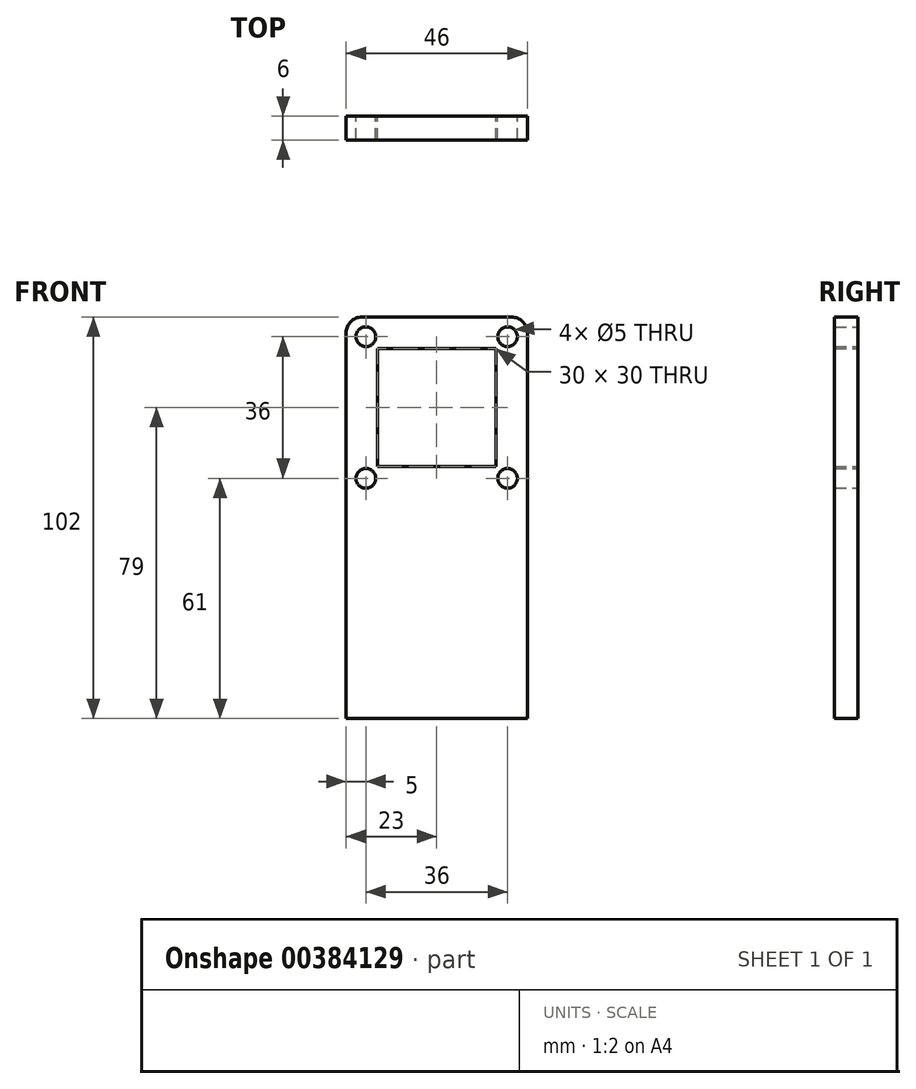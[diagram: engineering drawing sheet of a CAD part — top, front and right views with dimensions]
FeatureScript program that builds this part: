
annotation { "Feature Type Name" : "Feature", "Feature Type Description" : "" }
export const myFeature = defineFeature(function(context is Context, id is Id, definition is map)
    precondition{}
    {
        {
            var Q0;
            Q0=qCreatedBy(makeId("Front.planeOp"),FACE);
            var sketch = newSketch(context, id + "F0", { "sketchPlane" : qUnion([Q0])});
            skLineSegment(sketch, "E0.bottom", {"start": v(19, 51) * mm, "end": v(-19, 51) * mm});
            skLineSegment(sketch, "E0.top", {"start": v(23, -51) * mm, "end": v(-23, -51) * mm});
            skLineSegment(sketch, "E0.left", {"start": v(23, 47) * mm, "end": v(23, -51) * mm});
            skLineSegment(sketch, "E0.right", {"start": v(-23, 47) * mm, "end": v(-23, -51) * mm});
            skPoint(sketch, "E0.middle", {"position": v(0, 0) * mm});
            skLineSegment(sketch, "E1.bottom", {"start": v(15, 43) * mm, "end": v(-15, 43) * mm});
            skLineSegment(sketch, "E1.top", {"start": v(15, 13) * mm, "end": v(-15, 13) * mm});
            skLineSegment(sketch, "E1.left", {"start": v(15, 43) * mm, "end": v(15, 13) * mm});
            skLineSegment(sketch, "E1.right", {"start": v(-15, 43) * mm, "end": v(-15, 13) * mm});
            skPoint(sketch, "E1.middle", {"position": v(0, 28) * mm});
            skCircle(sketch, "E2", {"center": v(-18, 46) * mm, "radius": 2.5 * mm});
            skPoint(sketch, "E3.visualSharp", {"position": v(-23, 51) * mm});
            skArc(sketch, "E3.filletArc", {"start": v(-19, 51) * mm, "mid": v(-21.83, 49.83) * mm, "end": v(-23, 47) * mm});
            skPoint(sketch, "E4.visualSharp", {"position": v(23, 51) * mm});
            skArc(sketch, "E4.filletArc", {"start": v(23, 47) * mm, "mid": v(21.83, 49.83) * mm, "end": v(19, 51) * mm});
            skCircle(sketch, "E5.0.1.0", {"center": v(-18, 10) * mm, "radius": 2.5 * mm});
            skCircle(sketch, "E5.1.0.0", {"center": v(18, 46) * mm, "radius": 2.5 * mm});
            skCircle(sketch, "E5.1.1.0", {"center": v(18, 10) * mm, "radius": 2.5 * mm});
            skLineSegment(sketch, "E5.direction1", {"start": v(-18, 46) * mm, "end": v(18, 46) * mm, "construction": true});
            skLineSegment(sketch, "E5.direction2", {"start": v(-18, 46) * mm, "end": v(-18, 10) * mm, "construction": true});
            skSolve(sketch);
        }
        {
            var Q0;
            Q0=makeQuery(id+"F0.imprint","IMPRINT",FACE,{"disambiguationData":[TD([[makeQuery(id+"F0.imprint","IMPRINT",EDGE,{"derivedFrom":sQuery(id+"F0.wireOp",EDGE,"E0.bottom")}),1.0]])]});
            extrude(context, id + "F1", {"entities" : qUnion([Q0]), "depth" : 6 * mm});
        }
    });
